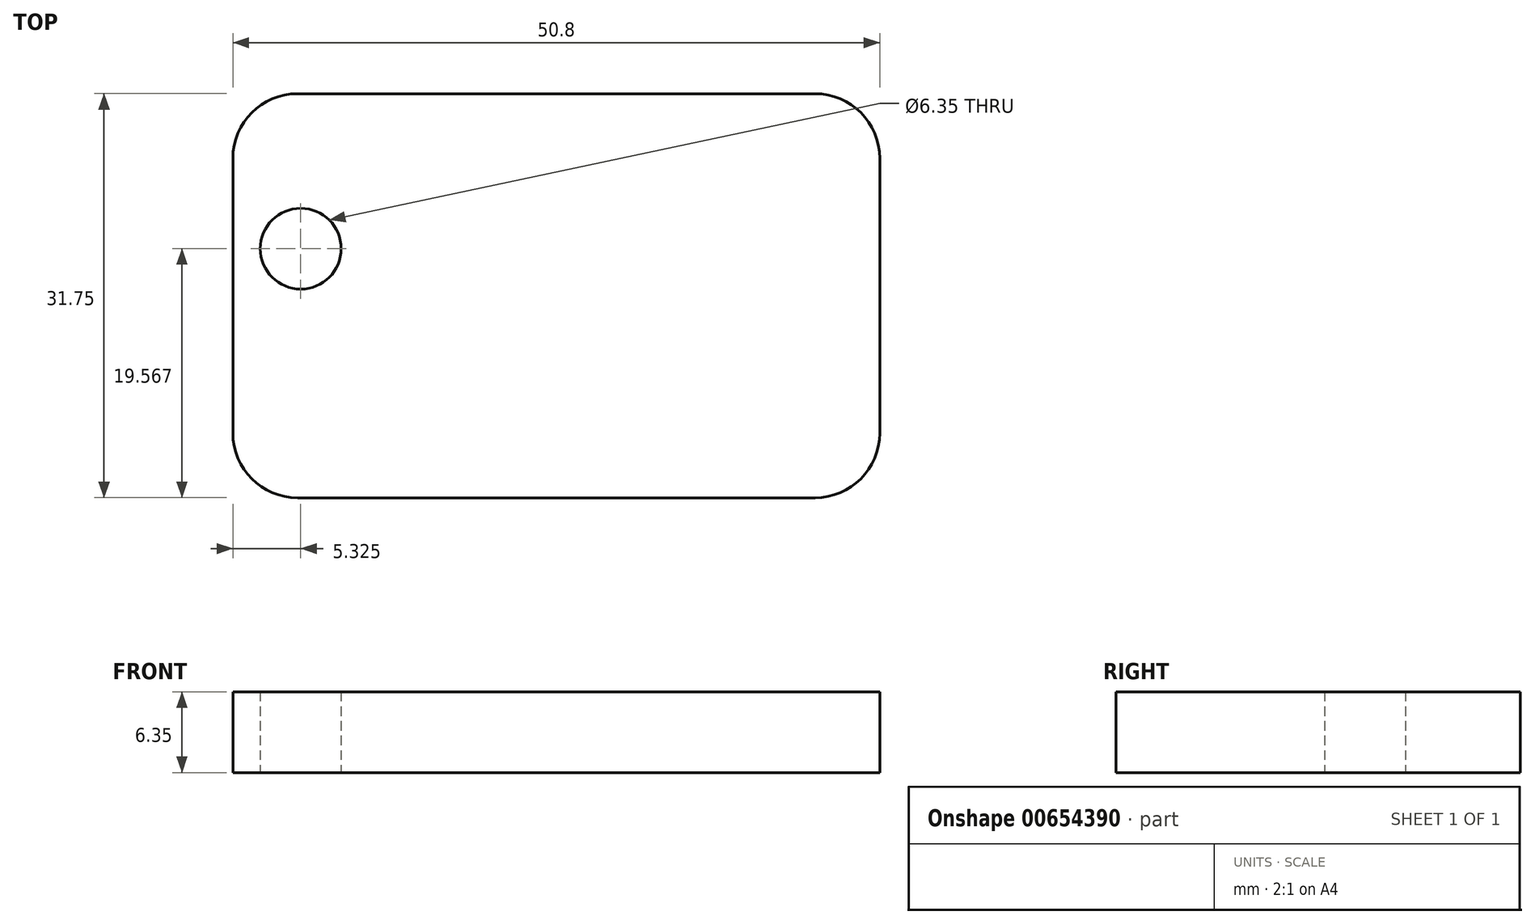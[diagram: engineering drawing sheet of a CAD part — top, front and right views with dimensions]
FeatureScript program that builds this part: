
annotation { "Feature Type Name" : "Feature", "Feature Type Description" : "" }
export const myFeature = defineFeature(function(context is Context, id is Id, definition is map)
    precondition{}
    {
        {
            var Q0;
            Q0=qCreatedBy(makeId("Top.planeOp"),FACE);
            var sketch = newSketch(context, id + "F0", { "sketchPlane" : qUnion([Q0])});
            skLineSegment(sketch, "E0.bottom", {"start": v(4.82, 2.47) * mm, "end": v(55.62, 2.47) * mm});
            skLineSegment(sketch, "E0.top", {"start": v(4.82, -29.28) * mm, "end": v(55.62, -29.28) * mm});
            skLineSegment(sketch, "E0.left", {"start": v(4.82, 2.47) * mm, "end": v(4.82, -29.28) * mm});
            skLineSegment(sketch, "E0.right", {"start": v(55.62, 2.47) * mm, "end": v(55.62, -29.28) * mm});
            skCircle(sketch, "E1", {"center": v(127.32, -81.53) * mm, "radius": 4.72 * mm});
            skCircle(sketch, "E2", {"center": v(10.15, -9.71) * mm, "radius": 3.18 * mm});
            skCircle(sketch, "E3", {"center": v(140.33, -91.78) * mm, "radius": 8.43 * mm});
            skCircle(sketch, "E4", {"center": v(148.74, -91.2) * mm, "radius": 10.12 * mm});
            skSolve(sketch);
        }
        {
            var Q0;
            Q0=makeQuery(id+"F0.imprint","IMPRINT",FACE,{"disambiguationData":[TD([[makeQuery(id+"F0.imprint","IMPRINT",EDGE,{"derivedFrom":sQuery(id+"F0.wireOp",EDGE,"E0.bottom")}),-1.0]])]});
            extrude(context, id + "F1", {"entities" : qUnion([Q0]), "depth" : 6.35 * mm, "offsetDistance" : 25.4 * mm});
        }
        {
            var Q0;
            Q0=makeQuery(id+"F1.opExtrude","SWEPT_EDGE",EDGE,{"disambiguationData":[OSD([sQuery(id+"F0.wireOp",EDGE,"E0.bottom"),sQuery(id+"F0.wireOp",EDGE,"E0.left")])]});
            var Q1;
            Q1=makeQuery(id+"F1.opExtrude","SWEPT_EDGE",EDGE,{"disambiguationData":[OSD([sQuery(id+"F0.wireOp",EDGE,"E0.bottom"),sQuery(id+"F0.wireOp",EDGE,"E0.right")])]});
            var Q2;
            Q2=makeQuery(id+"F1.opExtrude","SWEPT_EDGE",EDGE,{"disambiguationData":[OSD([sQuery(id+"F0.wireOp",EDGE,"E0.top"),sQuery(id+"F0.wireOp",EDGE,"E0.left")])]});
            var Q3;
            Q3=makeQuery(id+"F1.opExtrude","SWEPT_EDGE",EDGE,{"disambiguationData":[OSD([sQuery(id+"F0.wireOp",EDGE,"E0.top"),sQuery(id+"F0.wireOp",EDGE,"E0.right")])]});
            fillet(context, id + "F2", {"entities" : qUnion([Q0, Q1, Q2, Q3]), "radius" : 5.08 * mm, "tangentPropagation" : true, "allowEdgeOverflow" : false});
        }
    });
